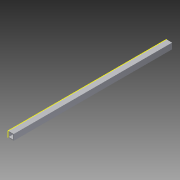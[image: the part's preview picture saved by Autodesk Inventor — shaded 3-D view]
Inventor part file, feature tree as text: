
AUTODESK INVENTOR PART (.ipt)
format: ipt  version: 2014 SP1 (Build 180222100, 222)  size: 86,016 bytes
history: native  units: in
note: dims shown in document units (in); Inventor stores cm internally (conversion verified against a paired STEP export)
features: sketch x2, extrude x1
ambient origin geometry x8: Origin, YZ Plane, XZ Plane, XY Plane, X Axis, Y Axis, Z Axis, Center Point
bodies: Solid1 (feature_tree)
feature tree (3):
  extrude  "Extrusion1"  Depth=1.0in
  sketch  "Sketch2"  dims[d2=0.125in d3=27.125in d4=0.0in]
  sketch  "Sketch1"  dims[d0=1.0in d1=1.0in]
